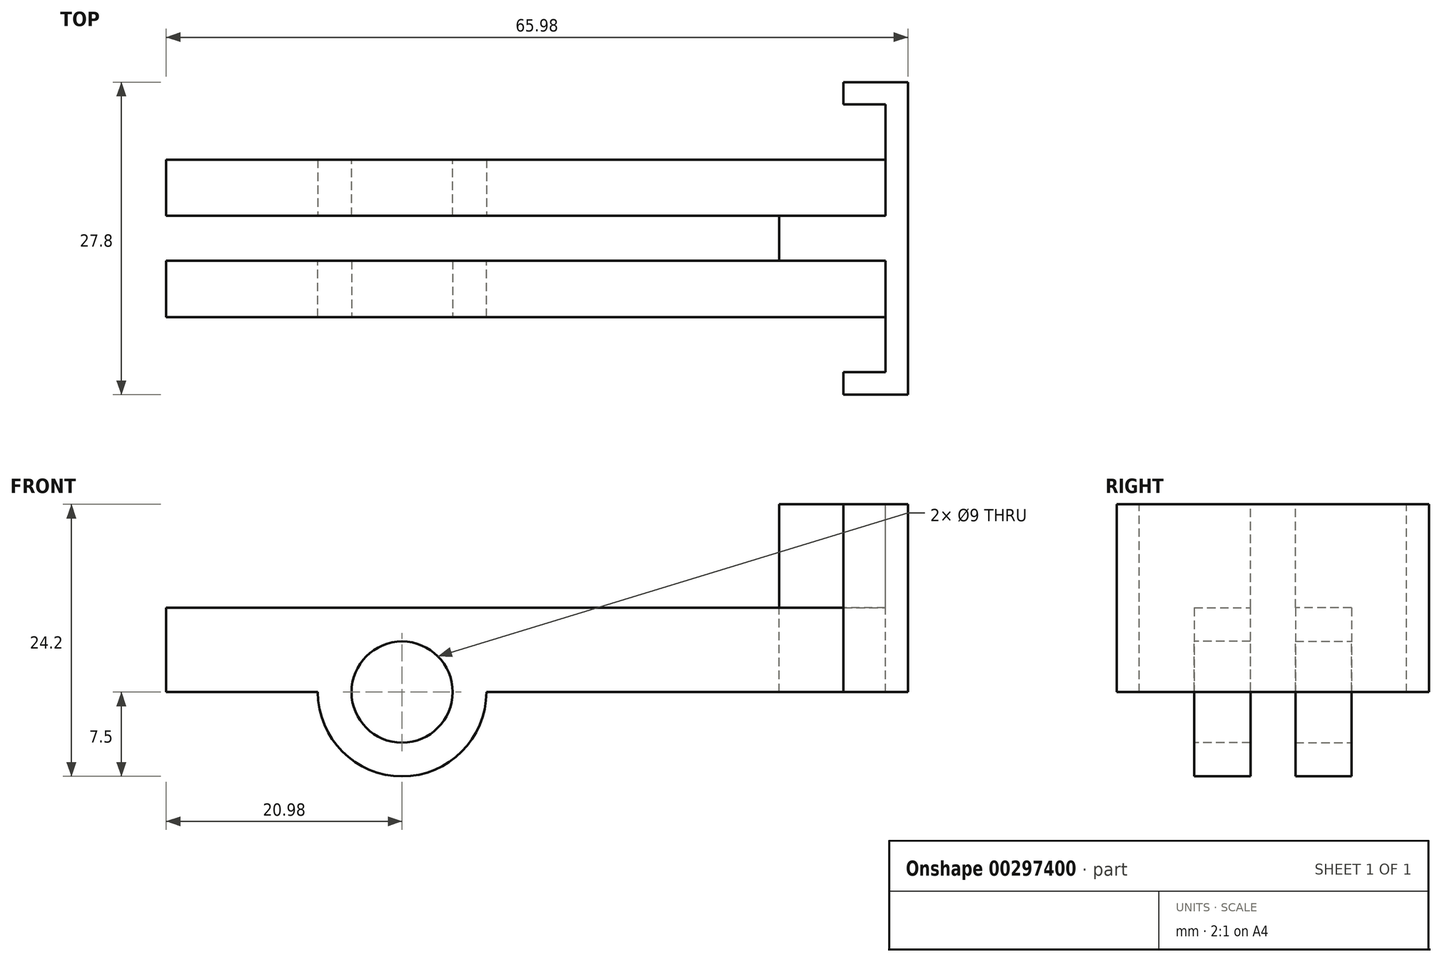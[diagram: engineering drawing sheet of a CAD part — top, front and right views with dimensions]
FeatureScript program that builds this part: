
annotation { "Feature Type Name" : "Feature", "Feature Type Description" : "" }
export const myFeature = defineFeature(function(context is Context, id is Id, definition is map)
    precondition{}
    {
        {
            var Q0;
            Q0=qCreatedBy(makeId("Front.planeOp"),FACE);
            var sketch = newSketch(context, id + "F0", { "sketchPlane" : qUnion([Q0])});
            skCircle(sketch, "E0", {"center": v(0, 0) * mm, "radius": 4.5 * mm});
            skCircle(sketch, "E1.0", {"center": v(0, 0) * mm, "radius": 7.5 * mm});
            skSolve(sketch);
        }
        {
            var Q0;
            Q0=makeQuery(id+"F0.imprint","IMPRINT",FACE,{"disambiguationData":[TD([[makeQuery(id+"F0.imprint","IMPRINT",EDGE,{"derivedFrom":sQuery(id+"F0.wireOp",EDGE,"E0")}),-1.0]])]});
            extrude(context, id + "F1", {"entities" : qUnion([Q0]), "depth" : 5 * mm});
        }
        {
            var Q0;
            Q0=makeQuery(id+"F1.opExtrude","CAP_FACE",FACE,{"disambiguationData":[OSD([sQuery(id+"F0.wireOp",EDGE,"E0"),sQuery(id+"F0.wireOp",EDGE,"E1.0")])],"isStart":false});
            var sketch = newSketch(context, id + "F2", { "sketchPlane" : qUnion([Q0])});
            skLineSegment(sketch, "E2.bottom", {"start": v(0, 0) * mm, "end": v(43, 0) * mm});
            skLineSegment(sketch, "E2.top", {"start": v(0, 7.5) * mm, "end": v(43, 7.5) * mm});
            skLineSegment(sketch, "E2.left", {"start": v(0, 0) * mm, "end": v(0, 7.5) * mm});
            skLineSegment(sketch, "E2.right", {"start": v(43, 0) * mm, "end": v(43, 7.5) * mm});
            skLineSegment(sketch, "E3.bottom", {"start": v(0, 7.5) * mm, "end": v(-20.98, 7.5) * mm});
            skLineSegment(sketch, "E3.top", {"start": v(0, 0) * mm, "end": v(-20.98, 0) * mm});
            skLineSegment(sketch, "E3.left", {"start": v(0, 7.5) * mm, "end": v(0, 0) * mm});
            skLineSegment(sketch, "E3.right", {"start": v(-20.98, 7.5) * mm, "end": v(-20.98, 0) * mm});
            skSolve(sketch);
        }
        {
            var Q0;
            {var subQ0=sQuery(id+"F2.wireOp",EDGE,"E3.bottom");Q0=makeQuery(id+"F2.imprint","IMPRINT",FACE,{"disambiguationData":[TD([[makeQuery(id+"F2.imprint","IMPRINT",EDGE,{"derivedFrom":subQ0}),1.0]])]});}
            var Q1;
            {var subQ4=sQuery(id+"F2.wireOp",EDGE,"E2.top");Q1=makeQuery(id+"F2.imprint","IMPRINT",FACE,{"disambiguationData":[TD([[makeQuery(id+"F2.imprint","IMPRINT",EDGE,{"derivedFrom":subQ4}),-1.0]])]});}
            extrude(context, id + "F3", {"entities" : qUnion([Q0, Q1]), "oppositeDirection" : true, "depth" : 5 * mm});
        }
        {
            var Q0;
            Q0=makeQuery(id+"F3.opExtrude","SWEPT_FACE",FACE,{"disambiguationData":[OSD([sQuery(id+"F2.wireOp",EDGE,"E2.right")])]});
            var sketch = newSketch(context, id + "F4", { "sketchPlane" : qUnion([Q0])});
            skLineSegment(sketch, "E4.bottom", {"start": v(-5, 0) * mm, "end": v(4.9, 0) * mm});
            skLineSegment(sketch, "E4.top", {"start": v(-5, 16.7) * mm, "end": v(4.9, 16.7) * mm});
            skLineSegment(sketch, "E4.left", {"start": v(-5, 0) * mm, "end": v(-5, 16.7) * mm});
            skLineSegment(sketch, "E4.right", {"start": v(4.9, 0) * mm, "end": v(4.9, 16.7) * mm});
            skSolve(sketch);
        }
        {
            var Q0;
            {var subQ3=sQuery(id+"F4.wireOp",EDGE,"E4.top");Q0=makeQuery(id+"F4.imprint","IMPRINT",FACE,{"disambiguationData":[TD([[makeQuery(id+"F4.imprint","IMPRINT",EDGE,{"derivedFrom":subQ3}),-1.0]])]});}
            var Q1;
            {var subQ3=sQuery(id+"F2.wireOp",EDGE,"E2.right");var subQ4=makeQuery(id+"F3.opExtrude","CAP_EDGE",EDGE,{"disambiguationData":[OSD([subQ3])],"isStart":false});Q1=makeQuery(id+"F4.imprint","IMPRINT",FACE,{"disambiguationData":[TD([[makeQuery(id+"F4.imprint","IMPRINT",EDGE,{"derivedFrom":subQ4}),1.0]])]});}
            extrude(context, id + "F5", {"entities" : qUnion([Q0, Q1]), "operationType" : NewBodyOperationType.ADD, "depth" : 2 * mm});
        }
        {
            var Q0;
            Q0=makeQuery(id+"F5.opExtrude","SWEPT_FACE",FACE,{"disambiguationData":[OSD([sQuery(id+"F4.wireOp",EDGE,"E4.right")])]});
            var sketch = newSketch(context, id + "F6", { "sketchPlane" : qUnion([Q0])});
            skLineSegment(sketch, "E5.bottom", {"start": v(-45, 0) * mm, "end": v(-39.27, 0) * mm});
            skLineSegment(sketch, "E5.top", {"start": v(-45, 16.7) * mm, "end": v(-39.27, 16.7) * mm});
            skLineSegment(sketch, "E5.left", {"start": v(-45, 0) * mm, "end": v(-45, 16.7) * mm});
            skLineSegment(sketch, "E5.right", {"start": v(-39.27, 0) * mm, "end": v(-39.27, 16.7) * mm});
            skSolve(sketch);
        }
        {
            var Q0;
            {var subQ2=sQuery(id+"F6.wireOp",EDGE,"E5.right");Q0=makeQuery(id+"F6.imprint","IMPRINT",FACE,{"disambiguationData":[TD([[makeQuery(id+"F6.imprint","IMPRINT",EDGE,{"derivedFrom":subQ2}),1.0]])]});}
            var Q1;
            {var subQ2=sQuery(id+"F6.wireOp",EDGE,"E5.left");Q1=makeQuery(id+"F6.imprint","IMPRINT",FACE,{"disambiguationData":[TD([[makeQuery(id+"F6.imprint","IMPRINT",EDGE,{"derivedFrom":subQ2}),-1.0]])]});}
            extrude(context, id + "F7", {"entities" : qUnion([Q0, Q1]), "operationType" : NewBodyOperationType.ADD, "depth" : 2 * mm});
        }
        {
            var Q0;
            Q0=makeQuery(id+"F5.boolean.opBoolean","MERGE",FACE,{"derivedFrom":[makeQuery(id+"F3.opExtrude","CAP_FACE",FACE,{"disambiguationData":[OSD([sQuery(id+"F0.wireOp",EDGE,"E1.0"),sQuery(id+"F2.wireOp",EDGE,"E2.bottom"),sQuery(id+"F2.wireOp",EDGE,"E2.top"),sQuery(id+"F2.wireOp",EDGE,"E2.right")])],"isStart":true}),makeQuery(id+"F5.opExtrude","SWEPT_FACE",FACE,{"disambiguationData":[OSD([sQuery(id+"F4.wireOp",EDGE,"E4.left")])]})]});
            var sketch = newSketch(context, id + "F8", { "sketchPlane" : qUnion([Q0])});
            skLineSegment(sketch, "E6.bottom", {"start": v(45, 0) * mm, "end": v(33.55, 0) * mm});
            skLineSegment(sketch, "E6.top", {"start": v(45, 16.7) * mm, "end": v(33.55, 16.7) * mm});
            skLineSegment(sketch, "E6.left", {"start": v(45, 0) * mm, "end": v(45, 16.7) * mm});
            skLineSegment(sketch, "E6.right", {"start": v(33.55, 0) * mm, "end": v(33.55, 16.7) * mm});
            skSolve(sketch);
        }
        {
            var Q0;
            {var subQ1=makeQuery(id+"F5.opExtrude","CAP_EDGE",EDGE,{"disambiguationData":[OSD([sQuery(id+"F4.wireOp",EDGE,"E4.left")])],"isStart":true});Q0=makeQuery(id+"F8.imprint","IMPRINT",FACE,{"disambiguationData":[TD([[makeQuery(id+"F8.imprint","IMPRINT",EDGE,{"derivedFrom":subQ1}),1.0]])]});}
            var Q1;
            {var subQ1=sQuery(id+"F8.wireOp",EDGE,"E6.bottom");Q1=makeQuery(id+"F8.imprint","IMPRINT",FACE,{"disambiguationData":[TD([[makeQuery(id+"F8.imprint","IMPRINT",EDGE,{"derivedFrom":subQ1}),1.0]])]});}
            extrude(context, id + "F9", {"entities" : qUnion([Q0, Q1]), "operationType" : NewBodyOperationType.ADD, "depth" : 2 * mm});
        }
        {
            var Q0;
            Q0=makeQuery(id+"F3.opExtrude","SWEPT_BODY",BODY,{"disambiguationData":[OSD([sQuery(id+"F0.wireOp",EDGE,"E1.0"),sQuery(id+"F2.wireOp",EDGE,"E3.bottom"),sQuery(id+"F2.wireOp",EDGE,"E3.top"),sQuery(id+"F2.wireOp",EDGE,"E3.right")])]});
            var Q1;
            Q1=makeQuery(id+"F1.opExtrude","SWEPT_BODY",BODY,{"disambiguationData":[OSD([sQuery(id+"F0.wireOp",EDGE,"E0"),sQuery(id+"F0.wireOp",EDGE,"E1.0")])]});
            var Q2;
            Q2=makeQuery(id+"F3.opExtrude","SWEPT_BODY",BODY,{"disambiguationData":[OSD([sQuery(id+"F0.wireOp",EDGE,"E1.0"),sQuery(id+"F2.wireOp",EDGE,"E2.bottom"),sQuery(id+"F2.wireOp",EDGE,"E2.top"),sQuery(id+"F2.wireOp",EDGE,"E2.right")])]});
            var Q3;
            Q3=makeQuery(id+"F9.opExtrude","CAP_FACE",FACE,{"disambiguationData":[OSD([sQuery(id+"F8.wireOp",EDGE,"E6.bottom"),sQuery(id+"F8.wireOp",EDGE,"E6.top"),sQuery(id+"F8.wireOp",EDGE,"E6.left"),sQuery(id+"F8.wireOp",EDGE,"E6.right")])],"isStart":false});
            mirror(context, id + "F10", {"operationType" : NewBodyOperationType.ADD, "entities" : qUnion([Q0, Q1, Q2]), "mirrorPlane" : qUnion([Q3])});
        }
    });
